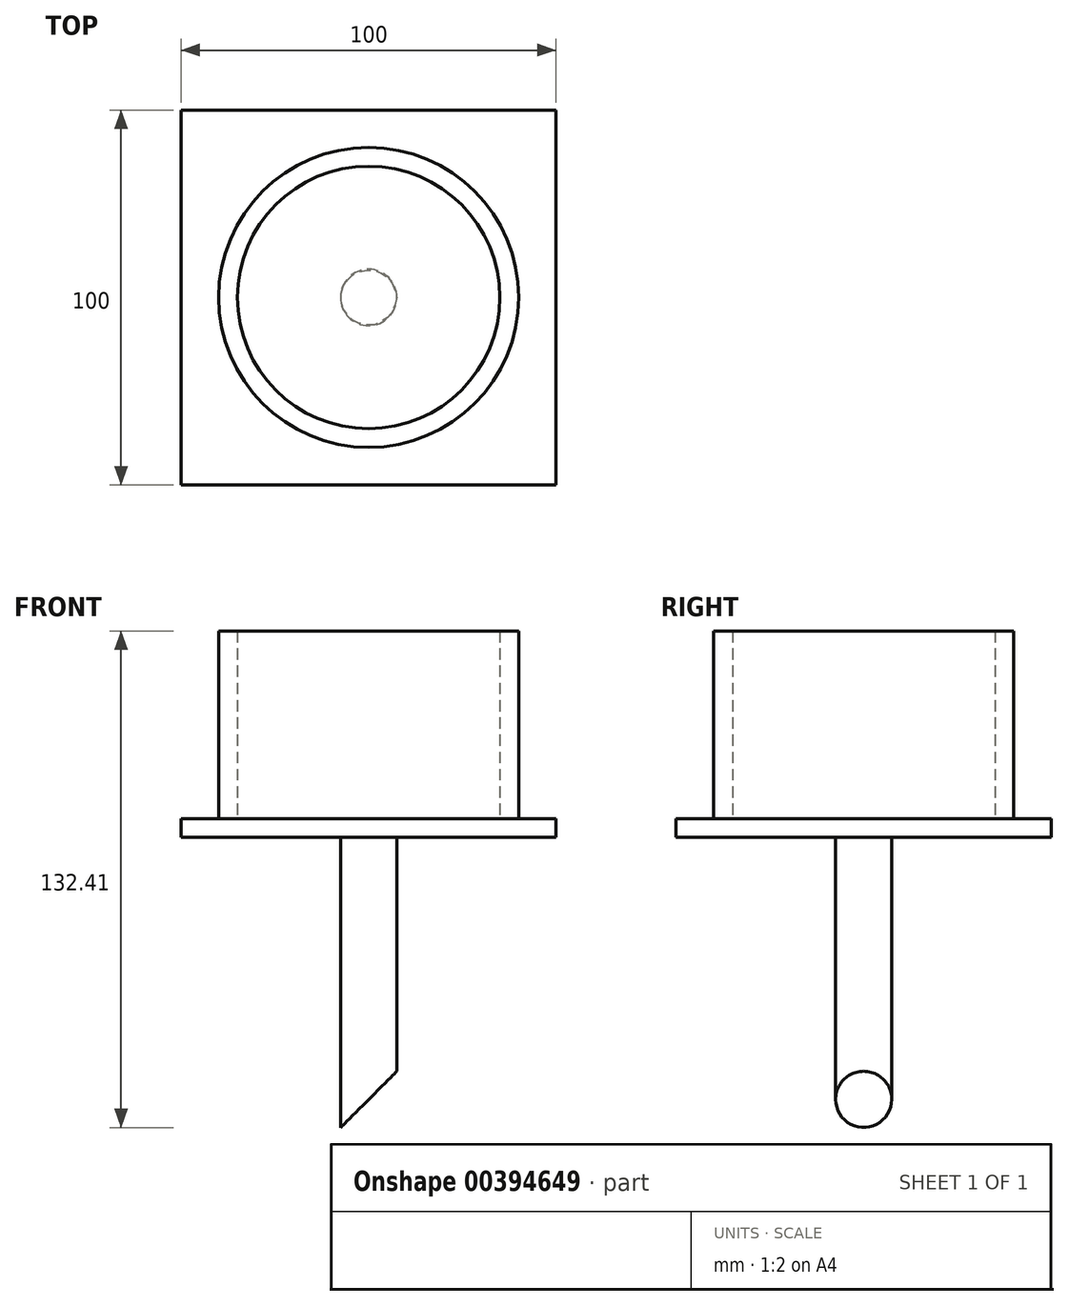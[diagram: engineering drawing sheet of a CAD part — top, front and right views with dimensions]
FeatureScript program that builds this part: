
annotation { "Feature Type Name" : "Feature", "Feature Type Description" : "" }
export const myFeature = defineFeature(function(context is Context, id is Id, definition is map)
    precondition{}
    {
        {
            var Q0;
            Q0=qCreatedBy(makeId("Top.planeOp"),FACE);
            var sketch = newSketch(context, id + "F0", { "sketchPlane" : qUnion([Q0])});
            skLineSegment(sketch, "E0.bottom", {"start": v(50, -50) * mm, "end": v(-50, -50) * mm});
            skLineSegment(sketch, "E0.top", {"start": v(50, 50) * mm, "end": v(-50, 50) * mm});
            skLineSegment(sketch, "E0.left", {"start": v(50, -50) * mm, "end": v(50, 50) * mm});
            skLineSegment(sketch, "E0.right", {"start": v(-50, -50) * mm, "end": v(-50, 50) * mm});
            skPoint(sketch, "E0.middle", {"position": v(0, 0) * mm});
            skCircle(sketch, "E1", {"center": v(0, 0) * mm, "radius": 40 * mm});
            skCircle(sketch, "E2", {"center": v(0, 0) * mm, "radius": 35 * mm});
            skSolve(sketch);
        }
        {
            var Q0;
            Q0=makeQuery(id+"F0.imprint","IMPRINT",FACE,{"disambiguationData":[TD([[makeQuery(id+"F0.imprint","IMPRINT",EDGE,{"derivedFrom":sQuery(id+"F0.wireOp",EDGE,"E0.bottom")}),-1.0]])]});
            var Q1;
            Q1=makeQuery(id+"F0.imprint","IMPRINT",FACE,{"disambiguationData":[TD([[makeQuery(id+"F0.imprint","IMPRINT",EDGE,{"derivedFrom":sQuery(id+"F0.wireOp",EDGE,"E1")}),1.0]])]});
            var Q2;
            Q2=makeQuery(id+"F0.imprint","IMPRINT",FACE,{"disambiguationData":[TD([[makeQuery(id+"F0.imprint","IMPRINT",EDGE,{"derivedFrom":sQuery(id+"F0.wireOp",EDGE,"E2")}),1.0]])]});
            extrude(context, id + "F1", {"entities" : qUnion([Q0, Q1, Q2]), "oppositeDirection" : true, "depth" : 5 * mm, "offsetDistance" : 25 * mm});
        }
        {
            var Q0;
            Q0=makeQuery(id+"F0.imprint","IMPRINT",FACE,{"disambiguationData":[TD([[makeQuery(id+"F0.imprint","IMPRINT",EDGE,{"derivedFrom":sQuery(id+"F0.wireOp",EDGE,"E1")}),1.0]])]});
            extrude(context, id + "F2", {"entities" : qUnion([Q0]), "operationType" : NewBodyOperationType.ADD, "depth" : 50 * mm, "offsetDistance" : 25 * mm});
        }
        {
            var Q0;
            Q0=makeQuery(id+"F1.opExtrude","CAP_FACE",FACE,{"disambiguationData":[OSD([sQuery(id+"F0.wireOp",EDGE,"E0.bottom"),sQuery(id+"F0.wireOp",EDGE,"E0.top"),sQuery(id+"F0.wireOp",EDGE,"E0.left"),sQuery(id+"F0.wireOp",EDGE,"E0.right")])],"isStart":false});
            var sketch = newSketch(context, id + "F3", { "sketchPlane" : qUnion([Q0])});
            skCircle(sketch, "E3", {"center": v(0, 0) * mm, "radius": 7.5 * mm});
            skSolve(sketch);
        }
        {
            var Q0;
            Q0=makeQuery(id+"F3.imprint","IMPRINT",FACE,{"disambiguationData":[TD([[makeQuery(id+"F3.imprint","IMPRINT",EDGE,{"derivedFrom":sQuery(id+"F3.wireOp",EDGE,"E3")}),1.0]])]});
            extrude(context, id + "F4", {"entities" : qUnion([Q0]), "operationType" : NewBodyOperationType.ADD, "depth" : 80 * mm, "offsetDistance" : 25 * mm});
        }
        {
            var Q0;
            Q0=qCreatedBy(makeId("Front.planeOp"),FACE);
            var sketch = newSketch(context, id + "F5", { "sketchPlane" : qUnion([Q0])});
            skLineSegment(sketch, "E4", {"start": v(13.1, -61.8) * mm, "end": v(-15.33, -90.24) * mm});
            skLineSegment(sketch, "E5", {"start": v(-15.33, -90.24) * mm, "end": v(13.1, -90.24) * mm});
            skLineSegment(sketch, "E6", {"start": v(13.1, -90.24) * mm, "end": v(13.1, -61.8) * mm});
            skSolve(sketch);
        }
        {
            var Q0;
            Q0=makeQuery(id+"F5.imprint","IMPRINT",FACE,{"disambiguationData":[TD([[makeQuery(id+"F5.imprint","IMPRINT",EDGE,{"derivedFrom":sQuery(id+"F5.wireOp",EDGE,"E4")}),1.0]])]});
            extrude(context, id + "F6", {"entities" : qUnion([Q0]), "endBound" : BoundingType.SYMMETRIC, "depth" : 50 * mm, "offsetDistance" : 25 * mm});
        }
        {
            var Q0;
            Q0=makeQuery(id+"F6.opExtrude","SWEPT_BODY",BODY,{"disambiguationData":[OSD([sQuery(id+"F5.wireOp",EDGE,"E4"),sQuery(id+"F5.wireOp",EDGE,"E5"),sQuery(id+"F5.wireOp",EDGE,"E6")])]});
            var Q1;
            Q1=makeQuery(id+"F1.opExtrude","SWEPT_BODY",BODY,{"disambiguationData":[OSD([sQuery(id+"F0.wireOp",EDGE,"E0.bottom"),sQuery(id+"F0.wireOp",EDGE,"E0.top"),sQuery(id+"F0.wireOp",EDGE,"E0.left"),sQuery(id+"F0.wireOp",EDGE,"E0.right")])]});
            booleanBodies(context, id + "F7", {"operationType" : BooleanOperationType.SUBTRACTION, "tools" : qUnion([Q0]), "targets" : qUnion([Q1])});
        }
    });
